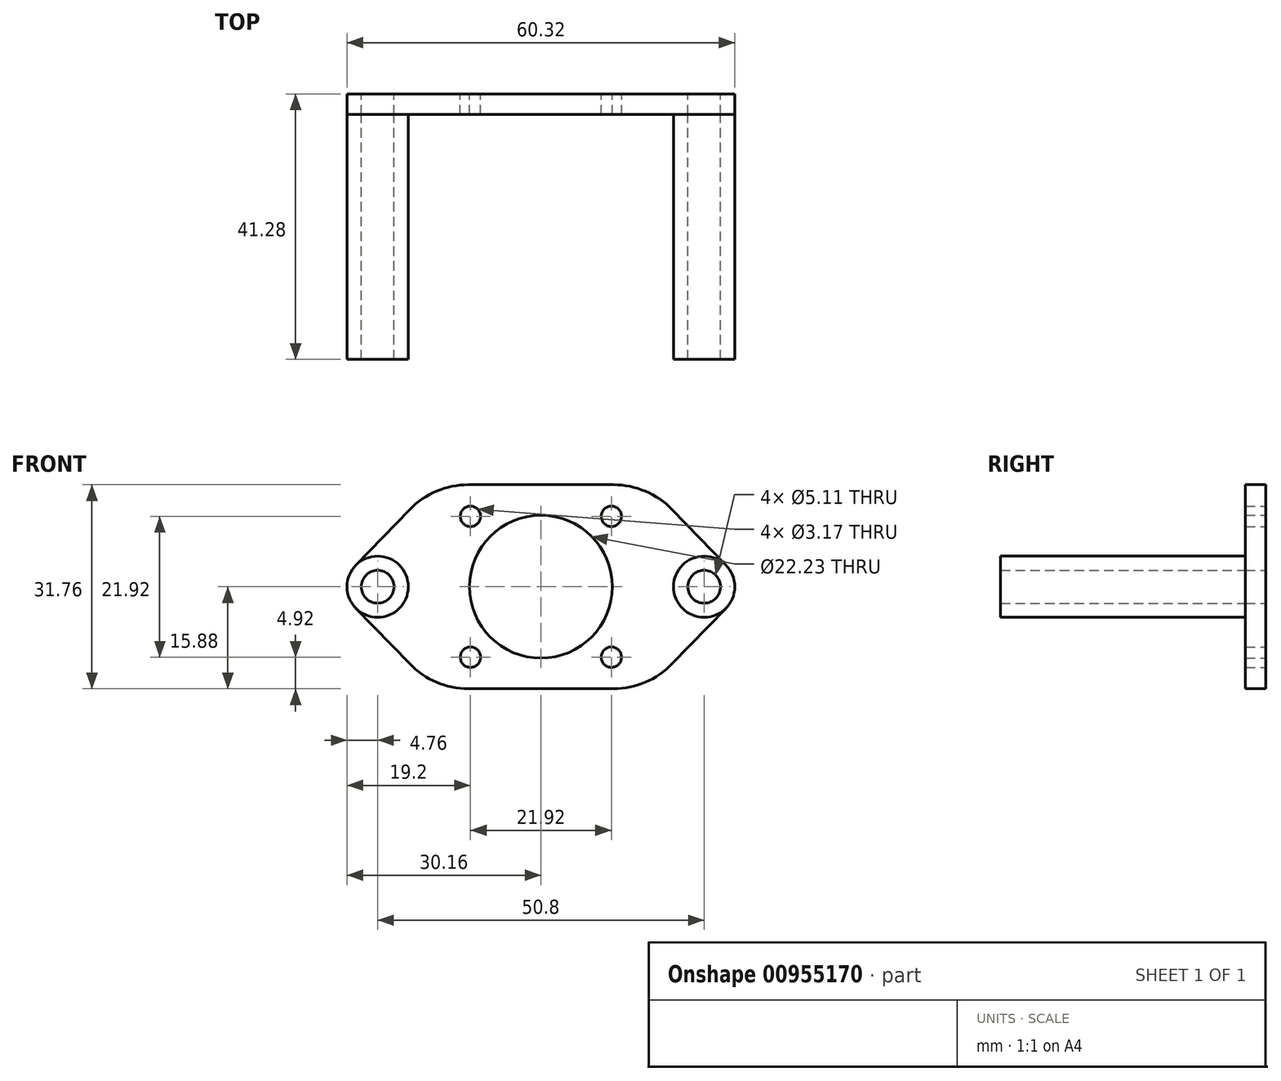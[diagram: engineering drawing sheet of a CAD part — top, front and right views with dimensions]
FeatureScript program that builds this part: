
annotation { "Feature Type Name" : "Feature", "Feature Type Description" : "" }
export const myFeature = defineFeature(function(context is Context, id is Id, definition is map)
    precondition{}
    {
        {
            var Q0;
            Q0=qCreatedBy(makeId("Front.planeOp"),FACE);
            var sketch = newSketch(context, id + "F0", { "sketchPlane" : qUnion([Q0])});
            skLineSegment(sketch, "E0", {"start": v(-25.4, 0) * mm, "end": v(0, 0) * mm, "construction": true});
            skLineSegment(sketch, "E1", {"start": v(25.4, 0) * mm, "end": v(0, 0) * mm, "construction": true});
            skCircle(sketch, "E2", {"center": v(-25.4, 0) * mm, "radius": 2.55 * mm});
            skCircle(sketch, "E3", {"center": v(25.4, 0) * mm, "radius": 2.55 * mm});
            skLineSegment(sketch, "E4.bottom", {"start": v(16.67, 15.88) * mm, "end": v(-16.67, 15.88) * mm, "construction": true});
            skLineSegment(sketch, "E4.top", {"start": v(16.67, -15.88) * mm, "end": v(-16.67, -15.88) * mm, "construction": true});
            skLineSegment(sketch, "E4.left", {"start": v(16.67, 15.88) * mm, "end": v(16.67, -15.88) * mm, "construction": true});
            skLineSegment(sketch, "E4.right", {"start": v(-16.67, 15.88) * mm, "end": v(-16.67, -15.88) * mm, "construction": true});
            skPoint(sketch, "E4.middle", {"position": v(0, 0) * mm});
            skLineSegment(sketch, "E5.bottom", {"start": v(10.96, 10.96) * mm, "end": v(-10.96, 10.96) * mm, "construction": true});
            skLineSegment(sketch, "E5.top", {"start": v(10.96, -10.96) * mm, "end": v(-10.96, -10.96) * mm, "construction": true});
            skLineSegment(sketch, "E5.left", {"start": v(10.96, 10.96) * mm, "end": v(10.96, -10.96) * mm, "construction": true});
            skLineSegment(sketch, "E5.right", {"start": v(-10.96, 10.96) * mm, "end": v(-10.96, -10.96) * mm, "construction": true});
            skCircle(sketch, "E6", {"center": v(10.96, 10.96) * mm, "radius": 1.59 * mm});
            skCircle(sketch, "E7", {"center": v(10.96, -10.96) * mm, "radius": 1.59 * mm});
            skCircle(sketch, "E8", {"center": v(-10.96, -10.96) * mm, "radius": 1.59 * mm});
            skCircle(sketch, "E9", {"center": v(-10.96, 10.96) * mm, "radius": 1.59 * mm});
            skArc(sketch, "E10", {"start": v(-28.82, 3.31) * mm, "mid": v(-30.16, 0) * mm, "end": v(-28.82, -3.31) * mm});
            skArc(sketch, "E11", {"start": v(28.82, 3.31) * mm, "mid": v(30.16, 0) * mm, "end": v(28.82, -3.31) * mm});
            skLineSegment(sketch, "E12", {"start": v(-28.82, 3.31) * mm, "end": v(-20.41, 12) * mm});
            skLineSegment(sketch, "E13", {"start": v(-28.82, -3.31) * mm, "end": v(-20.41, -12) * mm});
            skLineSegment(sketch, "E14", {"start": v(28.82, 3.31) * mm, "end": v(20.41, 12) * mm});
            skLineSegment(sketch, "E15", {"start": v(28.82, -3.31) * mm, "end": v(20.41, -12) * mm});
            skCircle(sketch, "E16", {"center": v(25.4, 0) * mm, "radius": 4.76 * mm, "construction": true});
            skCircle(sketch, "E17", {"center": v(-25.4, 0) * mm, "radius": 4.76 * mm, "construction": true});
            skLineSegment(sketch, "E18", {"start": v(-11.28, 15.88) * mm, "end": v(11.28, 15.88) * mm});
            skLineSegment(sketch, "E19", {"start": v(11.28, -15.88) * mm, "end": v(-11.28, -15.88) * mm});
            skPoint(sketch, "E20.visualSharp", {"position": v(-16.67, 15.88) * mm});
            skArc(sketch, "E20.filletArc", {"start": v(-11.28, 15.88) * mm, "mid": v(-16.24, 14.87) * mm, "end": v(-20.41, 12) * mm});
            skPoint(sketch, "E21.visualSharp", {"position": v(16.67, 15.88) * mm});
            skArc(sketch, "E21.filletArc", {"start": v(20.41, 12) * mm, "mid": v(16.24, 14.87) * mm, "end": v(11.28, 15.88) * mm});
            skPoint(sketch, "E22.visualSharp", {"position": v(16.67, -15.88) * mm});
            skArc(sketch, "E22.filletArc", {"start": v(11.28, -15.88) * mm, "mid": v(16.24, -14.87) * mm, "end": v(20.41, -12) * mm});
            skPoint(sketch, "E23.visualSharp", {"position": v(-16.67, -15.88) * mm});
            skArc(sketch, "E23.filletArc", {"start": v(-20.41, -12) * mm, "mid": v(-16.24, -14.87) * mm, "end": v(-11.28, -15.88) * mm});
            skCircle(sketch, "E24", {"center": v(0, 0) * mm, "radius": 11.11 * mm});
            skSolve(sketch);
        }
        {
            var Q0;
            Q0=makeQuery(id+"F0.imprint","IMPRINT",FACE,{"disambiguationData":[TD([[makeQuery(id+"F0.imprint","IMPRINT",EDGE,{"derivedFrom":sQuery(id+"F0.wireOp",EDGE,"E2")}),-1.0]])]});
            extrude(context, id + "F1", {"entities" : qUnion([Q0]), "depth" : 3.17 * mm, "offsetDistance" : 25.4 * mm});
        }
        {
            var Q0;
            Q0=makeQuery(id+"F1.opExtrude","CAP_FACE",FACE,{"disambiguationData":[OSD([sQuery(id+"F0.wireOp",EDGE,"E2"),sQuery(id+"F0.wireOp",EDGE,"E3"),sQuery(id+"F0.wireOp",EDGE,"E6"),sQuery(id+"F0.wireOp",EDGE,"E7"),sQuery(id+"F0.wireOp",EDGE,"E8"),sQuery(id+"F0.wireOp",EDGE,"E9"),sQuery(id+"F0.wireOp",EDGE,"E10"),sQuery(id+"F0.wireOp",EDGE,"E11"),sQuery(id+"F0.wireOp",EDGE,"E12"),sQuery(id+"F0.wireOp",EDGE,"E13"),sQuery(id+"F0.wireOp",EDGE,"E14"),sQuery(id+"F0.wireOp",EDGE,"E15"),sQuery(id+"F0.wireOp",EDGE,"E18"),sQuery(id+"F0.wireOp",EDGE,"E19"),sQuery(id+"F0.wireOp",EDGE,"E20.filletArc"),sQuery(id+"F0.wireOp",EDGE,"E21.filletArc"),sQuery(id+"F0.wireOp",EDGE,"E22.filletArc"),sQuery(id+"F0.wireOp",EDGE,"E23.filletArc"),sQuery(id+"F0.wireOp",EDGE,"E24")])],"isStart":false});
            var sketch = newSketch(context, id + "F2", { "sketchPlane" : qUnion([Q0])});
            skCircle(sketch, "E25", {"center": v(-25.4, 0) * mm, "radius": 4.76 * mm});
            skCircle(sketch, "E26", {"center": v(25.4, 0) * mm, "radius": 4.76 * mm});
            skCircle(sketch, "E27", {"center": v(-25.4, 0) * mm, "radius": 2.55 * mm});
            skCircle(sketch, "E28", {"center": v(25.4, 0) * mm, "radius": 2.55 * mm});
            skSolve(sketch);
        }
        {
            var Q0;
            Q0=qSketchRegion(id+"F2",true);
            extrude(context, id + "F3", {"entities" : qUnion([Q0]), "depth" : 38.1 * mm, "offsetDistance" : 25.4 * mm});
        }
    });
